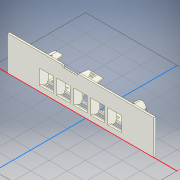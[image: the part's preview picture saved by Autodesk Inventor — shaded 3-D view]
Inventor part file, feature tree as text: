
AUTODESK INVENTOR PART (.ipt)
format: ipt  version: 2022 (Build 260153000, 153)  size: 388,096 bytes
history: native  units: mm
features: other x2, extrude x2, sketch x2
ambient origin geometry x8: Origin, YZ Plane, XZ Plane, XY Plane, X Axis, Y Axis, Z Axis, Center Point
bodies: Body1 (feature_tree)
feature tree (6):
  other  "Твердое тело1"
  extrude  "Выдавливание1"  Depth=17.135mm
  extrude  "Выдавливание2"  Depth=25.4mm TaperAngle=0.0deg
  sketch  "Эскиз1"
  sketch  "Эскиз2"
  other  "Cover Plate_1:1"
